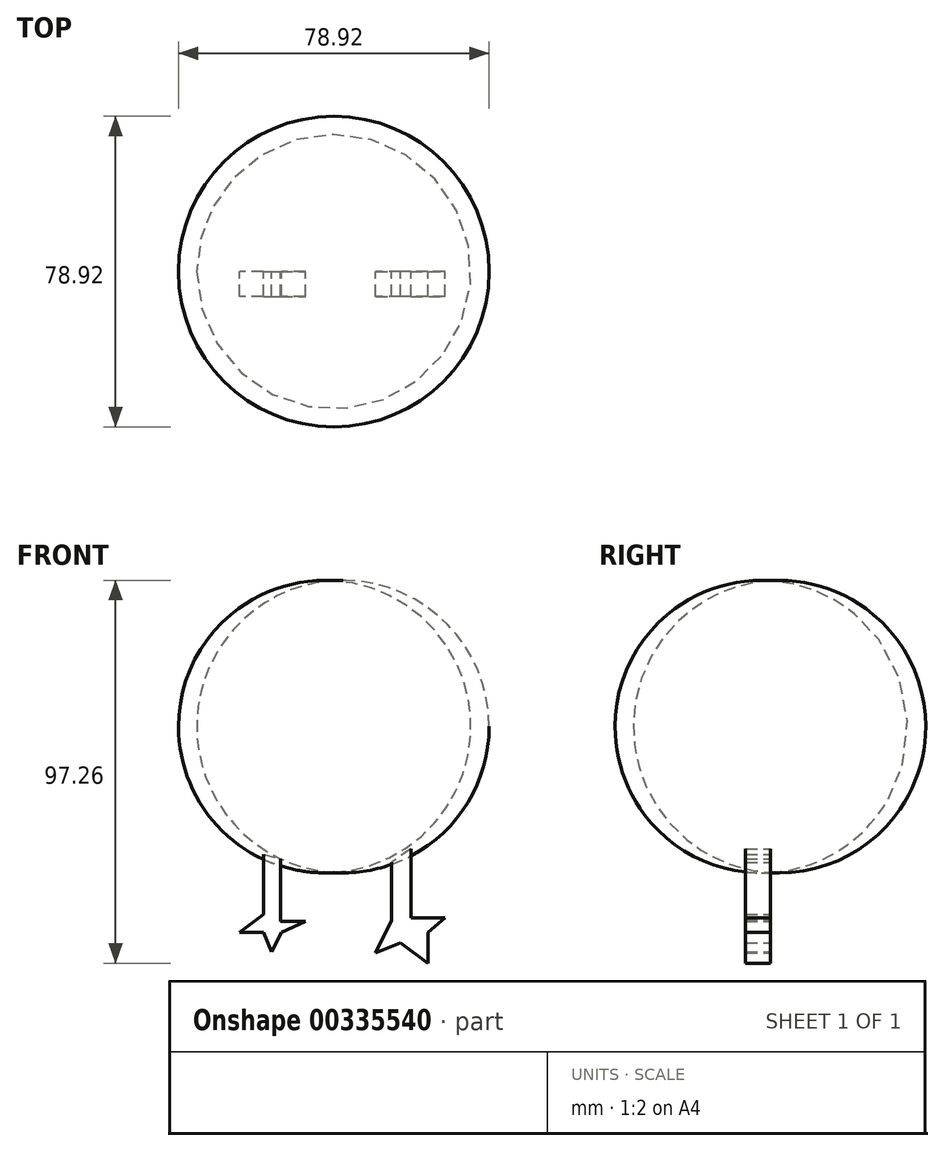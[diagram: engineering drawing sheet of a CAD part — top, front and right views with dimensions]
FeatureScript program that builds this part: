
annotation { "Feature Type Name" : "Feature", "Feature Type Description" : "" }
export const myFeature = defineFeature(function(context is Context, id is Id, definition is map)
    precondition{}
    {
        {
            var Q0;
            Q0=qCreatedBy(makeId("Front.planeOp"),FACE);
            var sketch = newSketch(context, id + "F0", { "sketchPlane" : qUnion([Q0])});
            skLineSegment(sketch, "E0", {"start": v(0, 36.46) * mm, "end": v(0, -37.68) * mm});
            skArc(sketch, "E1", {"start": v(0, -37.68) * mm, "mid": v(34.83, -0.61) * mm, "end": v(0, 36.46) * mm});
            skSolve(sketch);
        }
        {
            var Q0;
            Q0=makeQuery(id+"F0.imprint","IMPRINT",FACE,{"disambiguationData":[TD([[makeQuery(id+"F0.imprint","IMPRINT",EDGE,{"derivedFrom":sQuery(id+"F0.wireOp",EDGE,"E0")}),1.0]])]});
            var Q1;
            Q1=sQuery(id+"F0.wireOp",EDGE,"E0");
            revolve(context, id + "F1", {"entities" : qUnion([Q0]), "axis" : qUnion([Q1]), "revolveType" : RevolveType.FULL});
        }
        {
            var Q0;
            Q0=qCreatedBy(makeId("Front.planeOp"),FACE);
            var sketch = newSketch(context, id + "F2", { "sketchPlane" : qUnion([Q0])});
            skLineSegment(sketch, "E2", {"start": v(-17.84, -33.1) * mm, "end": v(-17.84, -48.35) * mm});
            skLineSegment(sketch, "E3", {"start": v(-13.53, -34.25) * mm, "end": v(-13.53, -50.08) * mm});
            skLineSegment(sketch, "E4", {"start": v(-17.84, -48.35) * mm, "end": v(-23.89, -52.96) * mm});
            skLineSegment(sketch, "E5", {"start": v(-17.84, -52.96) * mm, "end": v(-23.89, -52.96) * mm});
            skLineSegment(sketch, "E6", {"start": v(-17.84, -52.96) * mm, "end": v(-15.83, -57.85) * mm});
            skLineSegment(sketch, "E7", {"start": v(-15.83, -57.85) * mm, "end": v(-16.84, -55.4) * mm});
            skLineSegment(sketch, "E8", {"start": v(-15.83, -57.85) * mm, "end": v(-13.24, -52.96) * mm});
            skLineSegment(sketch, "E9", {"start": v(-13.53, -50.08) * mm, "end": v(-7.2, -50.08) * mm});
            skLineSegment(sketch, "E10", {"start": v(-7.2, -50.08) * mm, "end": v(-13.24, -52.96) * mm});
            skLineSegment(sketch, "E11", {"start": v(-17.84, -33.1) * mm, "end": v(-13.53, -34.25) * mm});
            skSolve(sketch);
        }
        {
            var Q0;
            Q0=makeQuery(id+"F2.imprint","IMPRINT",FACE,{"disambiguationData":[TD([[makeQuery(id+"F2.imprint","IMPRINT",EDGE,{"derivedFrom":sQuery(id+"F2.wireOp",EDGE,"E2")}),1.0]])]});
            extrude(context, id + "F3", {"entities" : qUnion([Q0]), "depth" : 6.35 * mm});
        }
        {
            var Q0;
            Q0=qCreatedBy(makeId("Front.planeOp"),FACE);
            var sketch = newSketch(context, id + "F4", { "sketchPlane" : qUnion([Q0])});
            skLineSegment(sketch, "E12", {"start": v(14.68, -35.11) * mm, "end": v(14.68, -49.8) * mm});
            skPoint(sketch, "E13.endSnap0", {"position": v(11.37, -49.8) * mm});
            skPoint(sketch, "E14.end.orphan", {"position": v(14.68, -53.82) * mm});
            skPoint(sketch, "E14.start.orphan", {"position": v(11.37, -53.82) * mm});
            skPoint(sketch, "E15.end.orphan", {"position": v(8.06, -49.8) * mm});
            skLineSegment(sketch, "E16", {"start": v(19.57, -31.66) * mm, "end": v(19.57, -49.21) * mm});
            skLineSegment(sketch, "E17", {"start": v(19.57, -31.66) * mm, "end": v(14.68, -35.11) * mm});
            skLineSegment(sketch, "E18", {"start": v(19.57, -49.21) * mm, "end": v(28.2, -49.21) * mm});
            skLineSegment(sketch, "E19", {"start": v(28.2, -49.21) * mm, "end": v(23.89, -52.96) * mm});
            skPoint(sketch, "E19.endSnap0", {"position": v(23.89, -49.21) * mm});
            skLineSegment(sketch, "E20", {"start": v(23.89, -52.96) * mm, "end": v(23.89, -60.73) * mm});
            skLineSegment(sketch, "E21", {"start": v(23.89, -60.73) * mm, "end": v(16.98, -55.55) * mm});
            skLineSegment(sketch, "E22", {"start": v(16.98, -55.55) * mm, "end": v(10.65, -58.14) * mm});
            skLineSegment(sketch, "E23", {"start": v(10.65, -58.14) * mm, "end": v(14.68, -49.8) * mm});
            skSolve(sketch);
        }
        {
            var Q0;
            Q0=makeQuery(id+"F4.imprint","IMPRINT",FACE,{"disambiguationData":[TD([[makeQuery(id+"F4.imprint","IMPRINT",EDGE,{"derivedFrom":sQuery(id+"F4.wireOp",EDGE,"E12")}),1.0]])]});
            extrude(context, id + "F5", {"entities" : qUnion([Q0]), "depth" : 6.35 * mm});
        }
    });
